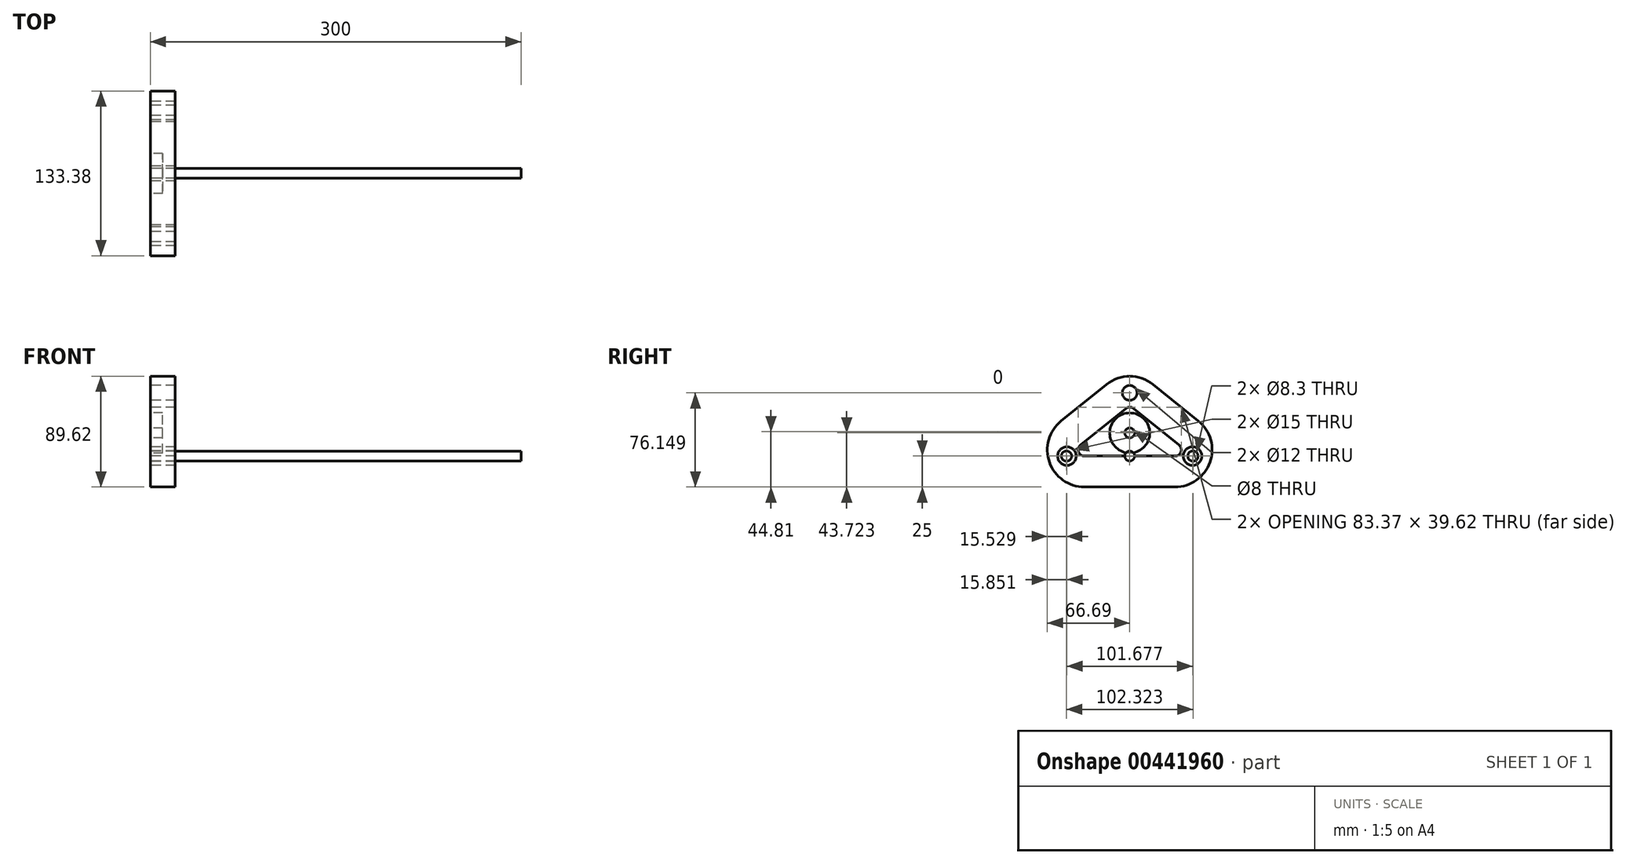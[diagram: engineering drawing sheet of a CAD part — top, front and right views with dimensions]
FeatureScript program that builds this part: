
annotation { "Feature Type Name" : "Feature", "Feature Type Description" : "" }
export const myFeature = defineFeature(function(context is Context, id is Id, definition is map)
    precondition{}
    {
        {
            var Q0;
            Q0=qCreatedBy(makeId("Right.planeOp"),FACE);
            var sketch = newSketch(context, id + "F0", { "sketchPlane" : qUnion([Q0])});
            skCircle(sketch, "E0", {"center": v(0, 0) * mm, "radius": 4 * mm});
            skSolve(sketch);
        }
        {
            var Q0;
            Q0 = qSketchRegion(id + "F0", true);
            extrude(context, id + "F1", {"entities" : qUnion([Q0]), "depth" : 300 * mm});
        }
        {
            var Q0;
            Q0=qCreatedBy(makeId("Right.planeOp"),FACE);
            var sketch = newSketch(context, id + "F2", { "sketchPlane" : qUnion([Q0])});
            skLineSegment(sketch, "E1", {"start": v(-3.14, 38.5) * mm, "end": v(-39.83, 8.9) * mm});
            skLineSegment(sketch, "E2", {"start": v(-36.69, 0) * mm, "end": v(0, 0) * mm});
            skLineSegment(sketch, "E3", {"start": v(0, 0) * mm, "end": v(36.69, 0) * mm});
            skLineSegment(sketch, "E4", {"start": v(39.83, 8.9) * mm, "end": v(3.14, 38.5) * mm});
            skPoint(sketch, "E5.visualSharp", {"position": v(-50.84, 0) * mm});
            skArc(sketch, "E5.filletArc", {"start": v(-39.83, 8.9) * mm, "mid": v(-41.4, 3.33) * mm, "end": v(-36.69, 0) * mm});
            skPoint(sketch, "E6.visualSharp", {"position": v(50.84, 0) * mm});
            skArc(sketch, "E6.filletArc", {"start": v(36.69, 0) * mm, "mid": v(41.4, 3.33) * mm, "end": v(39.83, 8.9) * mm});
            skPoint(sketch, "E7.visualSharp", {"position": v(0, 41.05) * mm});
            skArc(sketch, "E7.filletArc", {"start": v(3.14, 38.5) * mm, "mid": v(0, 39.62) * mm, "end": v(-3.14, 38.5) * mm});
            skCircle(sketch, "E8", {"center": v(-51.16, 0) * mm, "radius": 4.15 * mm});
            skCircle(sketch, "E9", {"center": v(50.84, 0) * mm, "radius": 7.5 * mm});
            skArc(sketch, "E10.0", {"start": v(36.69, -25) * mm, "mid": v(64.97, -5) * mm, "end": v(55.53, 28.34) * mm});
            skLineSegment(sketch, "E10.1", {"start": v(0, -25) * mm, "end": v(36.69, -25) * mm});
            skArc(sketch, "E10.2", {"start": v(18.85, 57.96) * mm, "mid": v(0, 64.62) * mm, "end": v(-18.85, 57.96) * mm});
            skLineSegment(sketch, "E10.3", {"start": v(-18.85, 57.96) * mm, "end": v(-55.53, 28.34) * mm});
            skArc(sketch, "E10.4", {"start": v(-55.53, 28.34) * mm, "mid": v(-64.97, -5) * mm, "end": v(-36.69, -25) * mm});
            skLineSegment(sketch, "E10.5", {"start": v(55.53, 28.34) * mm, "end": v(18.85, 57.96) * mm});
            skLineSegment(sketch, "E10.6", {"start": v(-36.69, -25) * mm, "end": v(0, -25) * mm});
            skCircle(sketch, "E11", {"center": v(0, 51.15) * mm, "radius": 6 * mm});
            skSolve(sketch);
        }
        {
            var Q0;
            Q0 = qSketchRegion(id + "F2", true);
            extrude(context, id + "F3", {"entities" : qUnion([Q0]), "depth" : 20 * mm});
        }
        {
            var Q0;
            Q0=makeQuery(id+"F3.opExtrude","SWEPT_BODY",BODY,{"disambiguationData":[OSD([sQuery(id+"F2.wireOp",EDGE,"E1"),sQuery(id+"F2.wireOp",EDGE,"E2"),sQuery(id+"F2.wireOp",EDGE,"E3"),sQuery(id+"F2.wireOp",EDGE,"E4"),sQuery(id+"F2.wireOp",EDGE,"E5.filletArc"),sQuery(id+"F2.wireOp",EDGE,"E6.filletArc"),sQuery(id+"F2.wireOp",EDGE,"E7.filletArc"),sQuery(id+"F2.wireOp",EDGE,"E8"),sQuery(id+"F2.wireOp",EDGE,"E9"),sQuery(id+"F2.wireOp",EDGE,"E10.0"),sQuery(id+"F2.wireOp",EDGE,"E10.1"),sQuery(id+"F2.wireOp",EDGE,"E10.2"),sQuery(id+"F2.wireOp",EDGE,"E10.3"),sQuery(id+"F2.wireOp",EDGE,"E10.4"),sQuery(id+"F2.wireOp",EDGE,"E10.5"),sQuery(id+"F2.wireOp",EDGE,"E10.6"),sQuery(id+"F2.wireOp",EDGE,"E11")])]});
            var Q1;
            Q1=qCreatedBy(makeId("Front.planeOp"),FACE);
            mirror(context, id + "F4", {"entities" : qUnion([Q0]), "mirrorPlane" : qUnion([Q1])});
        }
        {
            var Q0;
            Q0=qCreatedBy(makeId("Right.planeOp"),FACE);
            var sketch = newSketch(context, id + "F5", { "sketchPlane" : qUnion([Q0])});
            skCircle(sketch, "E12", {"center": v(0, 18.72) * mm, "radius": 16.22 * mm});
            skCircle(sketch, "E13", {"center": v(0, 18.72) * mm, "radius": 4 * mm});
            skSolve(sketch);
        }
        {
            var Q0;
            Q0 = qSketchRegion(id + "F5", true);
            extrude(context, id + "F6", {"entities" : qUnion([Q0]), "depth" : 10 * mm});
        }
    });
